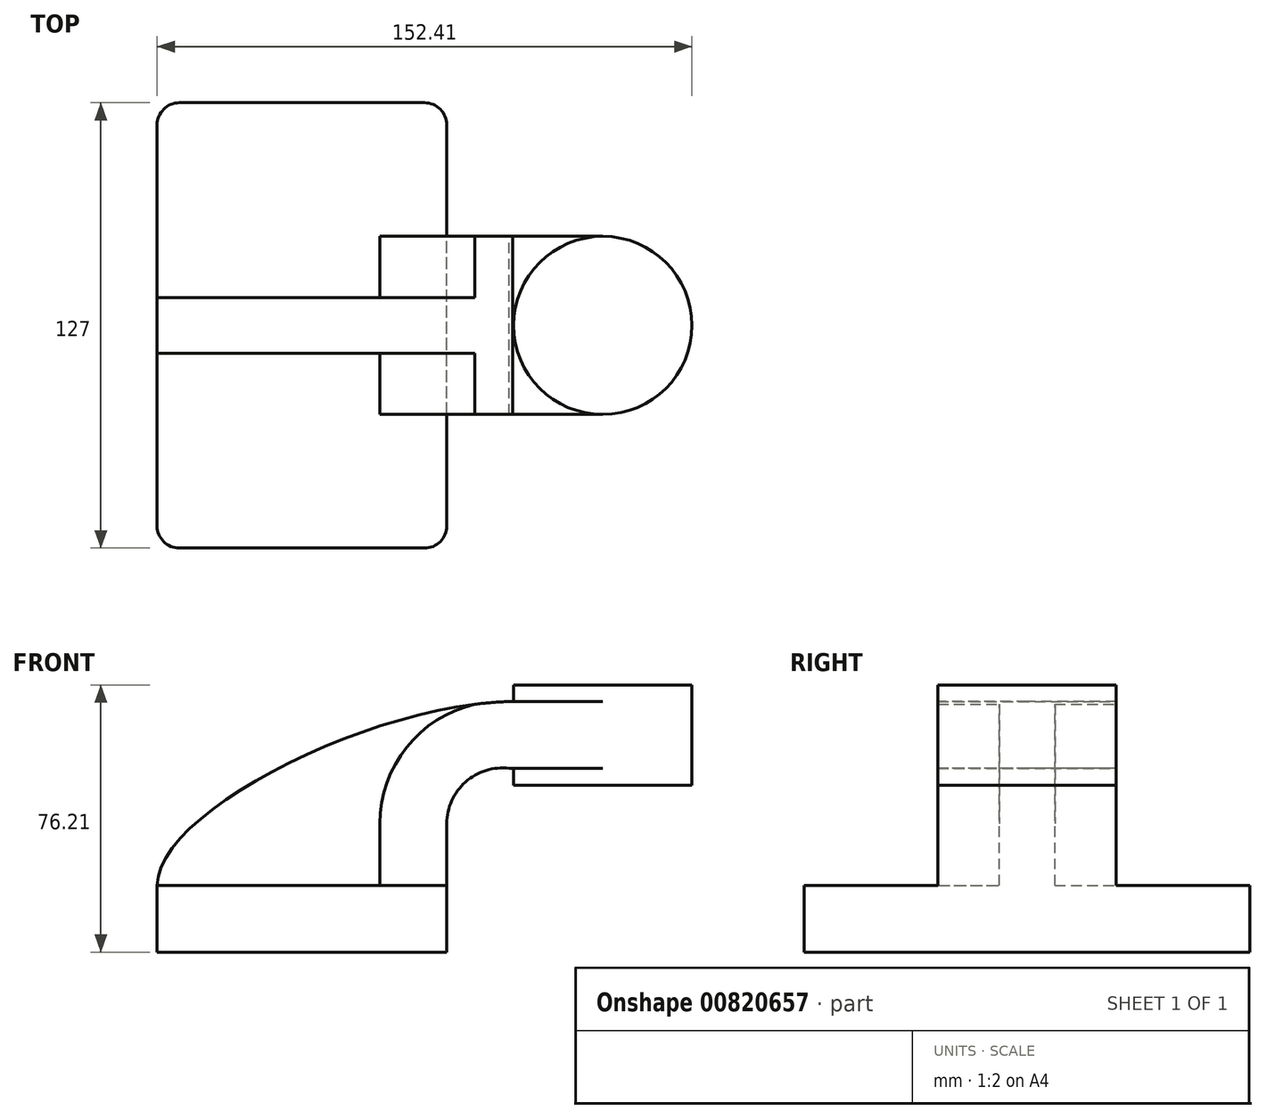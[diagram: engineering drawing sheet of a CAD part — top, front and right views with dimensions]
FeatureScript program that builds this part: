
annotation { "Feature Type Name" : "Feature", "Feature Type Description" : "" }
export const myFeature = defineFeature(function(context is Context, id is Id, definition is map)
    precondition{}
    {
        {
            var Q0;
            Q0=qCreatedBy(makeId("Front.planeOp"),FACE);
            var sketch = newSketch(context, id + "F0", { "sketchPlane" : qUnion([Q0])});
            skPoint(sketch, "E0.middle", {"position": v(0, 0) * mm});
            skLineSegment(sketch, "E1.bottom", {"start": v(41.28, -9.52) * mm, "end": v(-41.28, -9.53) * mm});
            skLineSegment(sketch, "E1.top", {"start": v(41.28, 9.53) * mm, "end": v(-41.28, 9.53) * mm});
            skLineSegment(sketch, "E1.left", {"start": v(41.28, -9.52) * mm, "end": v(41.28, 9.53) * mm});
            skLineSegment(sketch, "E1.right", {"start": v(-41.28, -9.53) * mm, "end": v(-41.28, 9.53) * mm});
            skLineSegment(sketch, "E2", {"start": v(41.28, 9.53) * mm, "end": v(41.28, 27.12) * mm});
            skLineSegment(sketch, "E3.bottom", {"start": v(111.12, 38.1) * mm, "end": v(60.32, 38.1) * mm});
            skLineSegment(sketch, "E3.top", {"start": v(111.12, 66.68) * mm, "end": v(60.32, 66.68) * mm});
            skLineSegment(sketch, "E3.left", {"start": v(111.12, 38.1) * mm, "end": v(111.12, 66.68) * mm});
            skLineSegment(sketch, "E3.right", {"start": v(60.32, 38.1) * mm, "end": v(60.32, 66.68) * mm});
            skPoint(sketch, "E3.middle", {"position": v(85.72, 52.39) * mm});
            skArc(sketch, "E4", {"start": v(41.27, 27.12) * mm, "mid": v(46.62, 39) * mm, "end": v(59.06, 42.88) * mm});
            skLineSegment(sketch, "E5", {"start": v(59.06, 42.88) * mm, "end": v(85.72, 42.88) * mm});
            skLineSegment(sketch, "E6.0", {"start": v(59.98, 61.93) * mm, "end": v(85.72, 61.93) * mm});
            skArc(sketch, "E6.1", {"start": v(22.23, 27.12) * mm, "mid": v(33.48, 52.8) * mm, "end": v(59.98, 61.93) * mm});
            skLineSegment(sketch, "E6.2", {"start": v(22.23, 9.53) * mm, "end": v(22.23, 27.12) * mm});
            skLineSegment(sketch, "E7", {"start": v(85.72, 38.1) * mm, "end": v(85.72, 66.68) * mm});
            skFitSpline(sketch, "E8", {"points": [v(-41.28, 9.53) * mm, v(59.98, 61.93) * mm], "startDerivative": vector(0, 62.84) * mm, "endDerivative": vector(120.94, 1.8) * mm});
            skSolve(sketch);
        }
        {
            var Q0;
            Q0=makeQuery(id+"F0.imprint","IMPRINT",FACE,{"disambiguationData":[TD([[makeQuery(id+"F0.imprint","IMPRINT",EDGE,{"derivedFrom":sQuery(id+"F0.wireOp",EDGE,"E1.bottom")}),-1.0]])]});
            extrude(context, id + "F1", {"entities" : qUnion([Q0]), "endBound" : BoundingType.SYMMETRIC, "depth" : 127 * mm, "offsetDistance" : 25.4 * mm});
        }
        {
            var Q0;
            {var subQ6=sQuery(id+"F0.wireOp",EDGE,"E2");Q0=makeQuery(id+"F0.imprint","IMPRINT",FACE,{"disambiguationData":[TD([[makeQuery(id+"F0.imprint","IMPRINT",EDGE,{"derivedFrom":subQ6}),1.0]])]});}
            var Q1;
            {var subQ0=sQuery(id+"F0.wireOp",EDGE,"E5");var subQ1=sQuery(id+"F0.wireOp",EDGE,"E3.right");var subQ2=makeQuery(id+"F0.imprint","INTERSECT",VERTEX,{"derivedFrom":[subQ1,subQ0]});Q1=makeQuery(id+"F0.imprint","IMPRINT",FACE,{"disambiguationData":[TD([[makeQuery(id+"F0.imprint","IMPRINT",EDGE,{"disambiguationData":[TD([[subQ2,-1.0]])],"derivedFrom":subQ1}),-1.0]])]});}
            extrude(context, id + "F2", {"entities" : qUnion([Q0, Q1]), "operationType" : NewBodyOperationType.ADD, "endBound" : BoundingType.SYMMETRIC, "depth" : 50.8 * mm, "offsetDistance" : 25.4 * mm});
        }
        {
            var Q0;
            {var subQ3=sQuery(id+"F0.wireOp",EDGE,"E6.2");Q0=makeQuery(id+"F0.imprint","IMPRINT",FACE,{"disambiguationData":[TD([[makeQuery(id+"F0.imprint","IMPRINT",EDGE,{"derivedFrom":subQ3}),1.0]])]});}
            extrude(context, id + "F3", {"entities" : qUnion([Q0]), "operationType" : NewBodyOperationType.ADD, "endBound" : BoundingType.SYMMETRIC, "depth" : 15.88 * mm, "offsetDistance" : 25.4 * mm});
        }
        {
            var Q0;
            {var subQ4=sQuery(id+"F0.wireOp",EDGE,"E3.left");Q0=makeQuery(id+"F0.imprint","IMPRINT",FACE,{"disambiguationData":[TD([[makeQuery(id+"F0.imprint","IMPRINT",EDGE,{"derivedFrom":subQ4}),1.0]])]});}
            var Q1;
            Q1=sQuery(id+"F0.wireOp",EDGE,"E7");
            revolve(context, id + "F4", {"operationType" : NewBodyOperationType.ADD, "surfaceOperationType" : NewSurfaceOperationType.NEW, "entities" : qUnion([Q0]), "axis" : qUnion([Q1]), "revolveType" : RevolveType.FULL});
        }
        {
            var Q0;
            Q0=makeQuery(id+"F1.opExtrude","CAP_EDGE",EDGE,{"disambiguationData":[OSD([sQuery(id+"F0.wireOp",EDGE,"E1.left")])],"isStart":false});
            var Q1;
            Q1=makeQuery(id+"F1.opExtrude","CAP_EDGE",EDGE,{"disambiguationData":[OSD([sQuery(id+"F0.wireOp",EDGE,"E1.right")])],"isStart":false});
            var Q2;
            Q2=makeQuery(id+"F1.opExtrude","CAP_EDGE",EDGE,{"disambiguationData":[OSD([sQuery(id+"F0.wireOp",EDGE,"E1.right")])],"isStart":true});
            var Q3;
            Q3=makeQuery(id+"F1.opExtrude","CAP_EDGE",EDGE,{"disambiguationData":[OSD([sQuery(id+"F0.wireOp",EDGE,"E1.left")])],"isStart":true});
            fillet(context, id + "F5", {"entities" : qUnion([Q0, Q1, Q2, Q3]), "radius" : 6.35 * mm, "tangentPropagation" : true, "allowEdgeOverflow" : false});
        }
    });
